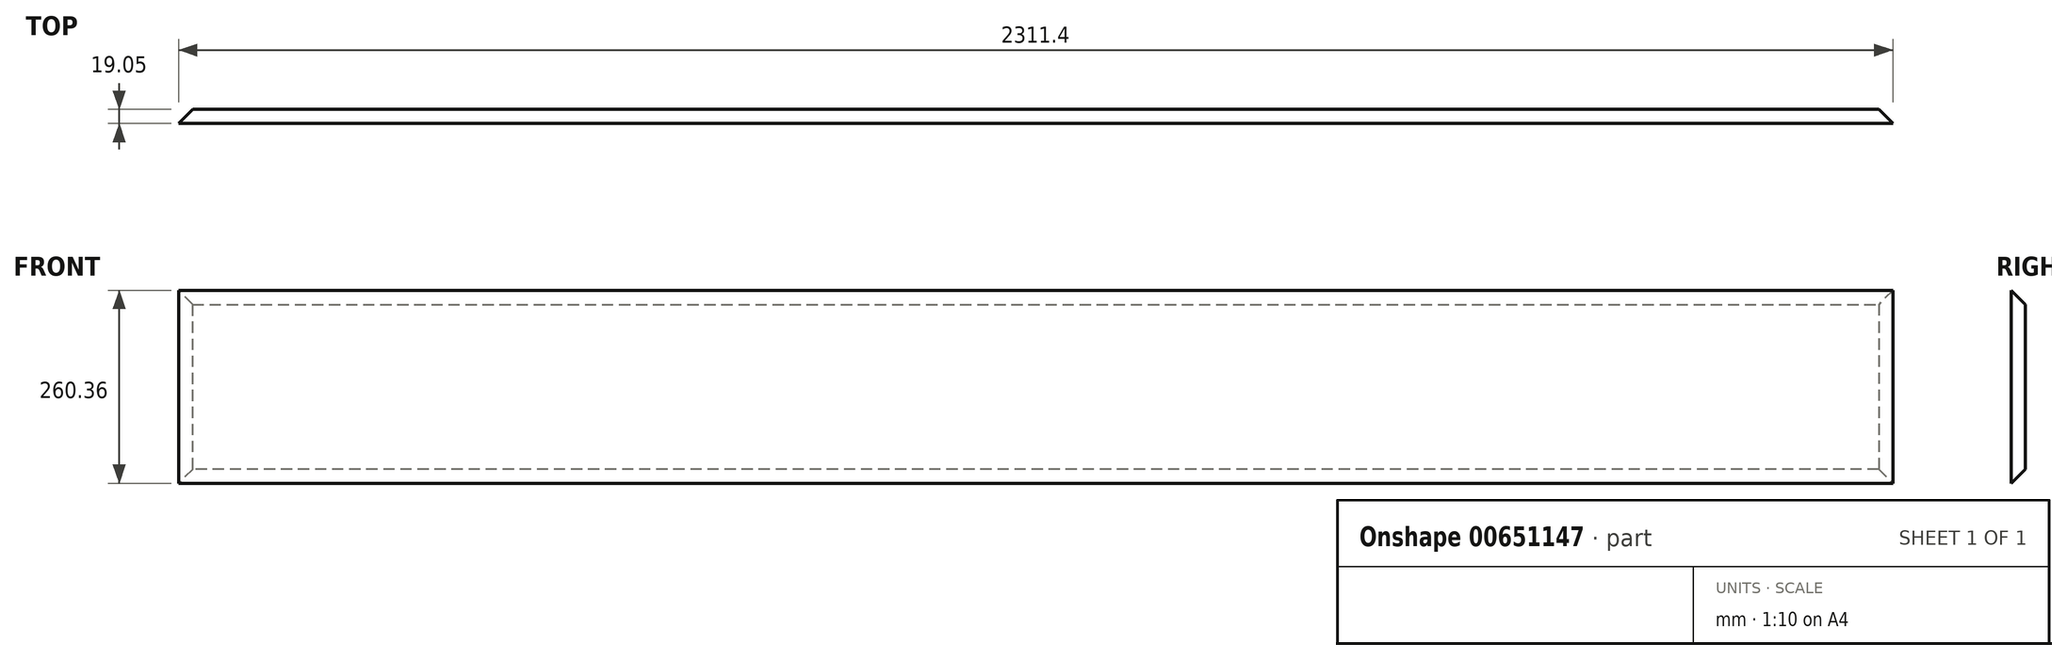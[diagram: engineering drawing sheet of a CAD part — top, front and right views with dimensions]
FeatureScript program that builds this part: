
annotation { "Feature Type Name" : "Feature", "Feature Type Description" : "" }
export const myFeature = defineFeature(function(context is Context, id is Id, definition is map)
    precondition{}
    {
        {
            var Q0;
            Q0=qCreatedBy(makeId("Front.planeOp"),FACE);
            var sketch = newSketch(context, id + "F0", { "sketchPlane" : qUnion([Q0])});
            skLineSegment(sketch, "E0.bottom", {"start": v(1155.7, 130.18) * mm, "end": v(-1155.7, 130.18) * mm});
            skLineSegment(sketch, "E0.top", {"start": v(1155.7, -130.17) * mm, "end": v(-1155.7, -130.17) * mm});
            skLineSegment(sketch, "E0.left", {"start": v(1155.7, 130.18) * mm, "end": v(1155.7, -130.17) * mm});
            skLineSegment(sketch, "E0.right", {"start": v(-1155.7, 130.18) * mm, "end": v(-1155.7, -130.17) * mm});
            skPoint(sketch, "E0.middle", {"position": v(0, 0) * mm});
            skSolve(sketch);
        }
        {
            var Q0;
            Q0 = qSketchRegion(id + "F0", true);
            extrude(context, id + "F1", {"entities" : qUnion([Q0]), "depth" : 19.05 * mm, "offsetDistance" : 25.4 * mm});
        }
        {
            var Q0;
            Q0=makeQuery(id+"F1.opExtrude","CAP_FACE",FACE,{"disambiguationData":[OSD([sQuery(id+"F0.wireOp",EDGE,"E0.bottom"),sQuery(id+"F0.wireOp",EDGE,"E0.top"),sQuery(id+"F0.wireOp",EDGE,"E0.left"),sQuery(id+"F0.wireOp",EDGE,"E0.right")])],"isStart":true});
            chamfer(context, id + "F2", {"entities" : qUnion([Q0]), "width" : 19.05 * mm, "tangentPropagation" : true});
        }
    });
